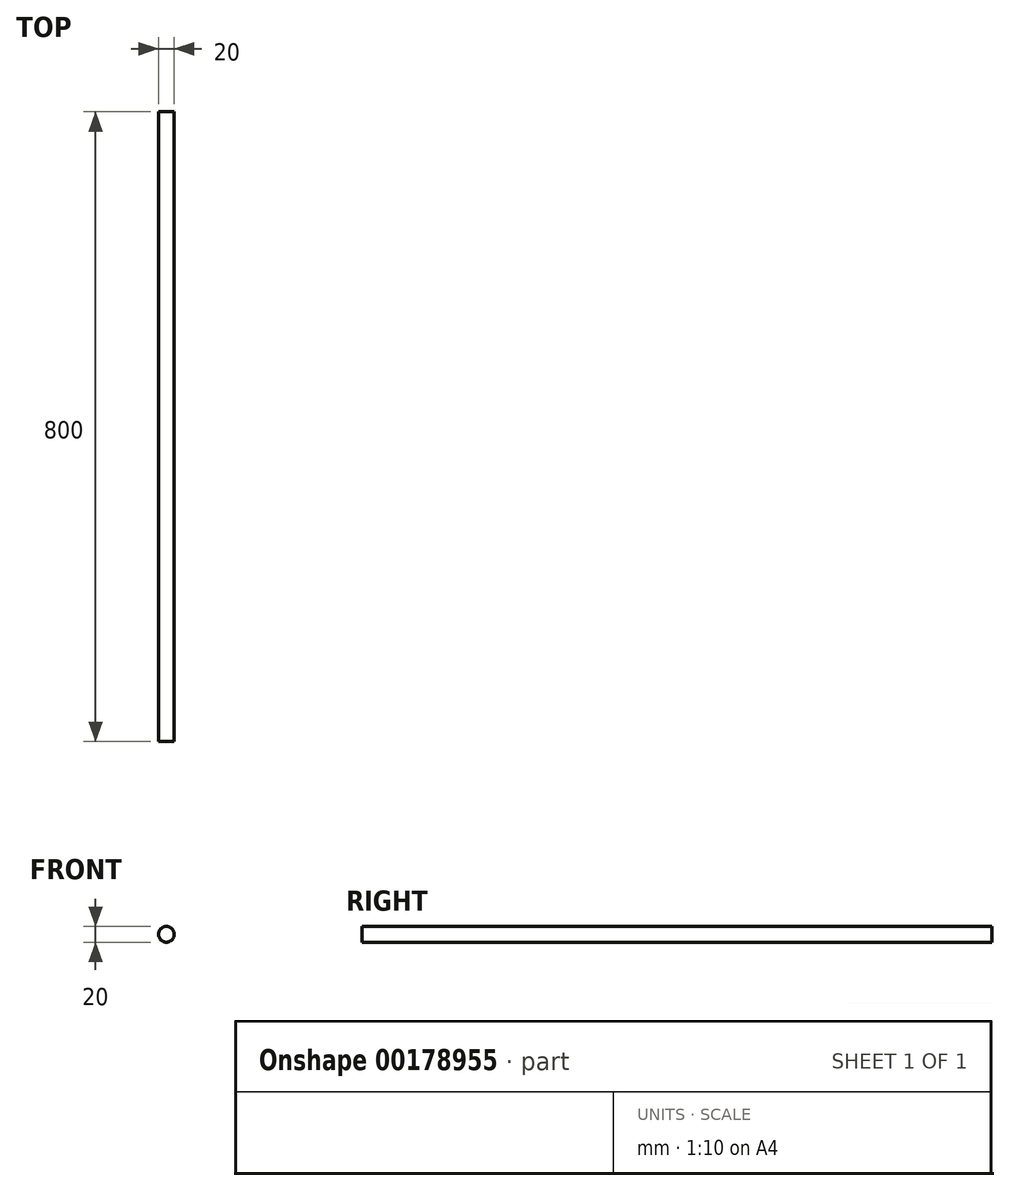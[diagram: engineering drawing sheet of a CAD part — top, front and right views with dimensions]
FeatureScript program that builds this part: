
annotation { "Feature Type Name" : "Feature", "Feature Type Description" : "" }
export const myFeature = defineFeature(function(context is Context, id is Id, definition is map)
    precondition{}
    {
        {
            var Q0;
            Q0=qCreatedBy(makeId("Front.planeOp"),FACE);
            var sketch = newSketch(context, id + "F0", { "sketchPlane" : qUnion([Q0])});
            skCircle(sketch, "E0", {"center": v(0, 0) * mm, "radius": 10 * mm});
            skSolve(sketch);
        }
        {
            var Q0;
            Q0=makeQuery(id+"F0.imprint","IMPRINT",FACE,{"disambiguationData":[TD([[makeQuery(id+"F0.imprint","IMPRINT",EDGE,{"derivedFrom":sQuery(id+"F0.wireOp",EDGE,"E0")}),1.0]])]});
            extrude(context, id + "F1", {"entities" : qUnion([Q0]), "depth" : 800 * mm});
        }
    });
